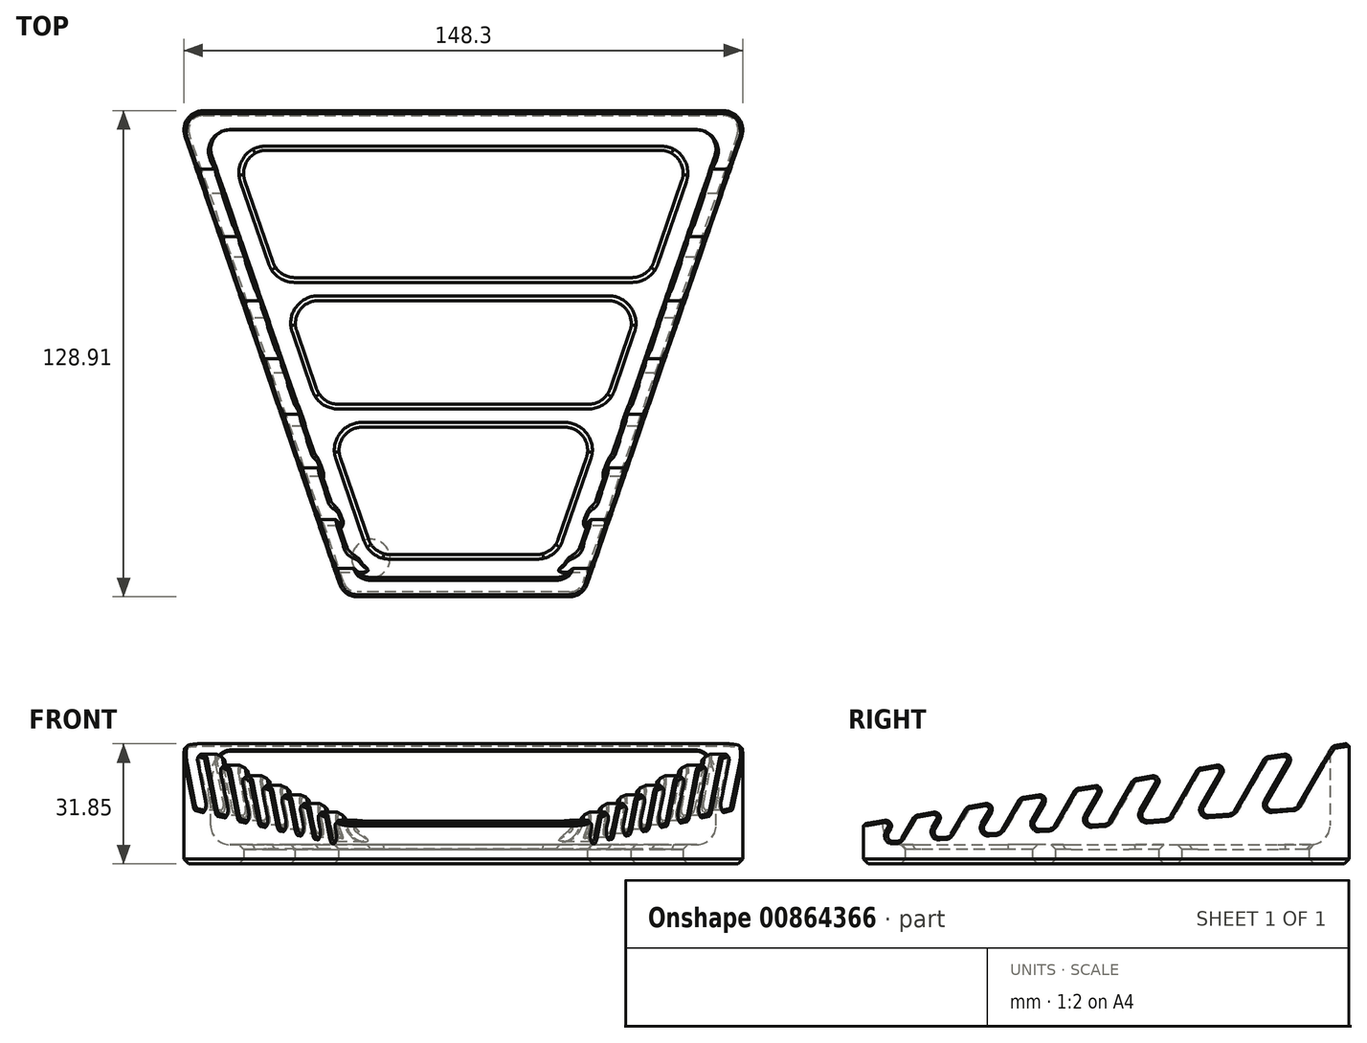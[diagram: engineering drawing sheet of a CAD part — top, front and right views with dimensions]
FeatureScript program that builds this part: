
annotation { "Feature Type Name" : "Feature", "Feature Type Description" : "" }
export const myFeature = defineFeature(function(context is Context, id is Id, definition is map)
    precondition{}
    {
        {
            var Q0;
            Q0=qCreatedBy(makeId("Top.planeOp"),FACE);
            var sketch = newSketch(context, id + "F0", { "sketchPlane" : qUnion([Q0])});
            skLineSegment(sketch, "E0", {"start": v(0, 200.12) * mm, "end": v(0, 0) * mm, "construction": true});
            skLineSegment(sketch, "E1", {"start": v(0, 0) * mm, "end": v(243.38, 0) * mm, "construction": true});
            skLineSegment(sketch, "E2", {"start": v(-76.2, 128.9) * mm, "end": v(76.2, 128.9) * mm});
            skLineSegment(sketch, "E3", {"start": v(76.2, 128.9) * mm, "end": v(31.75, 0) * mm});
            skLineSegment(sketch, "E4", {"start": v(31.75, 0) * mm, "end": v(-31.75, 0) * mm});
            skLineSegment(sketch, "E5", {"start": v(-31.75, 0) * mm, "end": v(-76.2, 128.9) * mm});
            skSolve(sketch);
        }
        {
            var Q0;
            Q0=makeQuery(id+"F0.imprint","IMPRINT",FACE,{"disambiguationData":[TD([[makeQuery(id+"F0.imprint","IMPRINT",EDGE,{"derivedFrom":sQuery(id+"F0.wireOp",EDGE,"E2")}),-1.0]])]});
            extrude(context, id + "F1", {"entities" : qUnion([Q0]), "depth" : 50.8 * mm, "offsetDistance" : 25.4 * mm});
        }
        {
            var Q0;
            Q0=qCreatedBy(makeId("Right.planeOp"),FACE);
            var sketch = newSketch(context, id + "F2", { "sketchPlane" : qUnion([Q0])});
            skLineSegment(sketch, "E6", {"start": v(0, 88.7) * mm, "end": v(0, 0) * mm, "construction": true});
            skLineSegment(sketch, "E7", {"start": v(0, 0) * mm, "end": v(187.78, 0) * mm, "construction": true});
            skCircle(sketch, "E8", {"center": v(114.24, 14.67) * mm, "radius": 14.67 * mm, "construction": true});
            skLineSegment(sketch, "E9", {"start": v(114.24, 14.67) * mm, "end": v(5.71, 5.71) * mm, "construction": true});
            skLineSegment(sketch, "E10", {"start": v(10.17, 2.13) * mm, "end": v(103.03, 5.2) * mm, "construction": true});
            skCircle(sketch, "E11", {"center": v(5.72, 5.71) * mm, "radius": 5.72 * mm, "construction": true});
            skLineSegment(sketch, "E12", {"start": v(111.83, 29.14) * mm, "end": v(4.78, 11.35) * mm, "construction": true});
            skSolve(sketch);
        }
        {
            var Q0;
            Q0=makeQuery(id+"F1.opExtrude","CAP_FACE",FACE,{"disambiguationData":[OSD([sQuery(id+"F0.wireOp",EDGE,"E2"),sQuery(id+"F0.wireOp",EDGE,"E3"),sQuery(id+"F0.wireOp",EDGE,"E4"),sQuery(id+"F0.wireOp",EDGE,"E5")])],"isStart":false});
            shell(context, id + "F3", {"entities" : qUnion([Q0]), "thickness" : 5.08 * mm});
        }
        {
            var Q0;
            Q0=makeQuery(id+"F3.opShell","OFFSET_EDGE",EDGE,{"disambiguationData":[OSD([sQuery(id+"F0.wireOp",EDGE,"E2"),sQuery(id+"F0.wireOp",EDGE,"E3")])]});
            var Q1;
            Q1=makeQuery(id+"F3.opShell","OFFSET_EDGE",EDGE,{"disambiguationData":[OSD([sQuery(id+"F0.wireOp",EDGE,"E3"),sQuery(id+"F0.wireOp",EDGE,"E4")])]});
            var Q2;
            Q2=makeQuery(id+"F3.opShell","OFFSET_EDGE",EDGE,{"disambiguationData":[OSD([sQuery(id+"F0.wireOp",EDGE,"E2"),sQuery(id+"F0.wireOp",EDGE,"E5")])]});
            var Q3;
            Q3=makeQuery(id+"F3.opShell","OFFSET_EDGE",EDGE,{"disambiguationData":[OSD([sQuery(id+"F0.wireOp",EDGE,"E4"),sQuery(id+"F0.wireOp",EDGE,"E5")])]});
            var Q4;
            Q4=makeQuery(id+"F1.opExtrude","SWEPT_EDGE",EDGE,{"disambiguationData":[OSD([sQuery(id+"F0.wireOp",EDGE,"E4"),sQuery(id+"F0.wireOp",EDGE,"E5")])]});
            var Q5;
            Q5=makeQuery(id+"F1.opExtrude","SWEPT_EDGE",EDGE,{"disambiguationData":[OSD([sQuery(id+"F0.wireOp",EDGE,"E3"),sQuery(id+"F0.wireOp",EDGE,"E4")])]});
            var Q6;
            Q6=makeQuery(id+"F1.opExtrude","SWEPT_EDGE",EDGE,{"disambiguationData":[OSD([sQuery(id+"F0.wireOp",EDGE,"E2"),sQuery(id+"F0.wireOp",EDGE,"E3")])]});
            var Q7;
            Q7=makeQuery(id+"F1.opExtrude","SWEPT_EDGE",EDGE,{"disambiguationData":[OSD([sQuery(id+"F0.wireOp",EDGE,"E2"),sQuery(id+"F0.wireOp",EDGE,"E5")])]});
            fillet(context, id + "F4", {"entities" : qUnion([Q0, Q1, Q2, Q3, Q4, Q5, Q6, Q7]), "radius" : 5.08 * mm, "tangentPropagation" : true, "allowEdgeOverflow" : false});
        }
        {
            var Q0;
            {var subQ0=sQuery(id+"F0.wireOp",EDGE,"E3");Q0=makeQuery(id+"F3.opShell","OFFSET_EDGE",EDGE,{"disambiguationData":[OSD([subQ0]),TDD([makeQuery(id+"F1.opExtrude","CAP_EDGE",EDGE,{"disambiguationData":[OSD([subQ0])],"isStart":true})])]});}
            fillet(context, id + "F5", {"entities" : qUnion([Q0]), "radius" : 5.08 * mm, "tangentPropagation" : true, "allowEdgeOverflow" : false});
        }
        {
            var Q0;
            Q0=qCreatedBy(makeId("Right.planeOp"),FACE);
            var sketch = newSketch(context, id + "F6", { "sketchPlane" : qUnion([Q0])});
            skLineSegment(sketch, "E13", {"start": v(0, 69.39) * mm, "end": v(0, 0) * mm, "construction": true});
            skLineSegment(sketch, "E14", {"start": v(0, 0) * mm, "end": v(193.07, 0) * mm, "construction": true});
            skLineSegment(sketch, "E15", {"start": v(14.91, 18.68) * mm, "end": v(7.52, 5.86) * mm, "construction": true});
            skLineSegment(sketch, "E16", {"start": v(28.35, 20.99) * mm, "end": v(20.22, 6.91) * mm, "construction": true});
            skLineSegment(sketch, "E17", {"start": v(42.35, 23.4) * mm, "end": v(33.46, 8) * mm, "construction": true});
            skLineSegment(sketch, "E18", {"start": v(56.86, 25.93) * mm, "end": v(47.17, 9.13) * mm, "construction": true});
            skLineSegment(sketch, "E19", {"start": v(71.98, 28.5) * mm, "end": v(61.49, 10.32) * mm, "construction": true});
            skLineSegment(sketch, "E20", {"start": v(88.27, 31.3) * mm, "end": v(76.89, 11.59) * mm, "construction": true});
            skLineSegment(sketch, "E21", {"start": v(105.77, 34.31) * mm, "end": v(93.44, 12.95) * mm, "construction": true});
            skLineSegment(sketch, "E22", {"start": v(121.34, 33.34) * mm, "end": v(110.38, 14.35) * mm, "construction": true});
            skLineSegment(sketch, "E23", {"start": v(124.53, 31.25) * mm, "end": v(141.6, 34.09) * mm});
            skLineSegment(sketch, "E24", {"start": v(141.6, 34.09) * mm, "end": v(141.6, 63.5) * mm});
            skLineSegment(sketch, "E25", {"start": v(141.6, 63.5) * mm, "end": v(-12.7, 63.5) * mm});
            skLineSegment(sketch, "E26", {"start": v(-12.7, 63.5) * mm, "end": v(-12.7, 8.45) * mm});
            skLineSegment(sketch, "E27", {"start": v(-12.7, 8.45) * mm, "end": v(8.88, 12.03) * mm});
            skLineSegment(sketch, "E28", {"start": v(124.53, 31.25) * mm, "end": v(115, 14.73) * mm});
            skLineSegment(sketch, "E29", {"start": v(115, 14.73) * mm, "end": v(105.76, 13.97) * mm});
            skLineSegment(sketch, "E30", {"start": v(105.76, 13.97) * mm, "end": v(114.8, 29.63) * mm});
            skLineSegment(sketch, "E31", {"start": v(106.69, 28.28) * mm, "end": v(98.06, 13.33) * mm});
            skLineSegment(sketch, "E32", {"start": v(98.06, 13.33) * mm, "end": v(88.82, 12.57) * mm});
            skLineSegment(sketch, "E33", {"start": v(88.82, 12.57) * mm, "end": v(96.96, 26.67) * mm});
            skLineSegment(sketch, "E34", {"start": v(88.85, 25.32) * mm, "end": v(81.12, 11.94) * mm});
            skLineSegment(sketch, "E35", {"start": v(81.12, 11.94) * mm, "end": v(72.65, 11.24) * mm});
            skLineSegment(sketch, "E36", {"start": v(72.65, 11.24) * mm, "end": v(79.93, 23.84) * mm});
            skLineSegment(sketch, "E37", {"start": v(71.82, 22.5) * mm, "end": v(64.95, 10.6) * mm});
            skLineSegment(sketch, "E38", {"start": v(64.95, 10.6) * mm, "end": v(58.02, 10.03) * mm});
            skLineSegment(sketch, "E39", {"start": v(58.02, 10.03) * mm, "end": v(64.52, 21.28) * mm});
            skLineSegment(sketch, "E40", {"start": v(50.32, 9.4) * mm, "end": v(44.01, 8.87) * mm});
            skLineSegment(sketch, "E41", {"start": v(44.01, 8.87) * mm, "end": v(49.76, 18.83) * mm});
            skLineSegment(sketch, "E42", {"start": v(41.65, 17.48) * mm, "end": v(36.31, 8.24) * mm});
            skLineSegment(sketch, "E43", {"start": v(36.31, 8.24) * mm, "end": v(30.61, 7.77) * mm});
            skLineSegment(sketch, "E44", {"start": v(30.61, 7.77) * mm, "end": v(35.64, 16.48) * mm});
            skLineSegment(sketch, "E45", {"start": v(27.53, 15.13) * mm, "end": v(22.91, 7.13) * mm});
            skLineSegment(sketch, "E46", {"start": v(22.91, 7.13) * mm, "end": v(17.53, 6.69) * mm});
            skLineSegment(sketch, "E47", {"start": v(17.53, 6.69) * mm, "end": v(21.86, 14.19) * mm});
            skLineSegment(sketch, "E48", {"start": v(13.75, 12.84) * mm, "end": v(9.83, 6.05) * mm});
            skLineSegment(sketch, "E49", {"start": v(9.83, 6.05) * mm, "end": v(8.1, 5.91) * mm});
            skLineSegment(sketch, "E50", {"start": v(6.66, 8.2) * mm, "end": v(8.88, 12.03) * mm});
            skLineSegment(sketch, "E51", {"start": v(13.75, 12.84) * mm, "end": v(21.86, 14.19) * mm});
            skLineSegment(sketch, "E52", {"start": v(27.53, 15.13) * mm, "end": v(35.64, 16.48) * mm});
            skLineSegment(sketch, "E53", {"start": v(41.65, 17.48) * mm, "end": v(49.76, 18.83) * mm});
            skLineSegment(sketch, "E54", {"start": v(56.4, 19.93) * mm, "end": v(64.52, 21.28) * mm});
            skLineSegment(sketch, "E55", {"start": v(71.82, 22.5) * mm, "end": v(79.93, 23.84) * mm});
            skLineSegment(sketch, "E56", {"start": v(88.85, 25.32) * mm, "end": v(96.96, 26.67) * mm});
            skLineSegment(sketch, "E57", {"start": v(106.69, 28.28) * mm, "end": v(114.8, 29.63) * mm});
            skLineSegment(sketch, "E58", {"start": v(56.4, 19.93) * mm, "end": v(50.32, 9.4) * mm});
            skPoint(sketch, "E59.visualSharp", {"position": v(5.2, 5.67) * mm});
            skArc(sketch, "E59.filletArc", {"start": v(6.66, 8.2) * mm, "mid": v(6.7, 6.62) * mm, "end": v(8.1, 5.91) * mm});
            skSolve(sketch);
        }
        {
            var Q0;
            Q0=qSketchRegion(id+"F6",true);
            extrude(context, id + "F7", {"entities" : qUnion([Q0]), "operationType" : NewBodyOperationType.REMOVE, "endBound" : BoundingType.THROUGH_ALL, "oppositeDirection" : true, "depth" : 25.4 * mm, "offsetDistance" : 25.4 * mm, "hasSecondDirection" : true, "secondDirectionBound" : SecondDirectionBoundingType.THROUGH_ALL, "secondDirectionOppositeDirection" : false, "secondDirectionDepth" : 25.4 * mm});
        }
        {
            var Q0;
            Q0=makeQuery(id+"F3.opShell","OFFSET_FACE",FACE,{"disambiguationData":[OSD([sQuery(id+"F0.wireOp",EDGE,"E2"),sQuery(id+"F0.wireOp",EDGE,"E3"),sQuery(id+"F0.wireOp",EDGE,"E4"),sQuery(id+"F0.wireOp",EDGE,"E5")])]});
            var sketch = newSketch(context, id + "F8", { "sketchPlane" : qUnion([Q0])});
            skLineSegment(sketch, "E60", {"start": v(-151.17, 0) * mm, "end": v(0, 0) * mm, "construction": true});
            skLineSegment(sketch, "E61", {"start": v(0, 0) * mm, "end": v(0, 307.09) * mm, "construction": true});
            skLineSegment(sketch, "E62", {"start": v(-23.78, 11.18) * mm, "end": v(23.78, 11.18) * mm});
            skLineSegment(sketch, "E63", {"start": v(23.78, 11.18) * mm, "end": v(35.43, 44.96) * mm});
            skLineSegment(sketch, "E64", {"start": v(60.77, 118.44) * mm, "end": v(-60.77, 118.44) * mm});
            skLineSegment(sketch, "E65", {"start": v(-60.77, 118.44) * mm, "end": v(-49.12, 84.65) * mm});
            skLineSegment(sketch, "E66", {"start": v(-36.48, 48) * mm, "end": v(36.48, 48) * mm, "construction": true});
            skLineSegment(sketch, "E67", {"start": v(-48.07, 81.6) * mm, "end": v(48.07, 81.6) * mm, "construction": true});
            skLineSegment(sketch, "E68", {"start": v(-35.43, 44.96) * mm, "end": v(35.43, 44.96) * mm});
            skLineSegment(sketch, "E69", {"start": v(-37.53, 51.05) * mm, "end": v(37.53, 51.05) * mm});
            skLineSegment(sketch, "E70", {"start": v(-47.02, 78.56) * mm, "end": v(47.02, 78.56) * mm});
            skLineSegment(sketch, "E71", {"start": v(-49.12, 84.65) * mm, "end": v(49.12, 84.65) * mm});
            skLineSegment(sketch, "E72.trimOffspring", {"start": v(-35.43, 44.96) * mm, "end": v(-23.78, 11.18) * mm});
            skLineSegment(sketch, "E73.trimOffspring", {"start": v(37.53, 51.05) * mm, "end": v(47.02, 78.56) * mm});
            skLineSegment(sketch, "E74.trimOffspring", {"start": v(49.12, 84.65) * mm, "end": v(60.77, 118.44) * mm});
            skLineSegment(sketch, "E75.trimOffspring", {"start": v(-47.02, 78.56) * mm, "end": v(-37.53, 51.05) * mm});
            skSolve(sketch);
        }
        {
            var Q0;
            Q0=makeQuery(id+"F8.imprint","IMPRINT",FACE,{"disambiguationData":[TD([[makeQuery(id+"F8.imprint","IMPRINT",EDGE,{"derivedFrom":sQuery(id+"F8.wireOp",EDGE,"E64")}),1.0]])]});
            var Q1;
            Q1=makeQuery(id+"F8.imprint","IMPRINT",FACE,{"disambiguationData":[TD([[makeQuery(id+"F8.imprint","IMPRINT",EDGE,{"derivedFrom":sQuery(id+"F8.wireOp",EDGE,"E69")}),1.0]])]});
            var Q2;
            Q2=makeQuery(id+"F8.imprint","IMPRINT",FACE,{"disambiguationData":[TD([[makeQuery(id+"F8.imprint","IMPRINT",EDGE,{"derivedFrom":sQuery(id+"F8.wireOp",EDGE,"E62")}),1.0]])]});
            extrude(context, id + "F9", {"entities" : qUnion([Q0, Q1, Q2]), "operationType" : NewBodyOperationType.REMOVE, "endBound" : BoundingType.THROUGH_ALL, "oppositeDirection" : true, "depth" : 25.4 * mm, "offsetDistance" : 25.4 * mm});
        }
        {
            var Q0;
            Q0=makeQuery(id+"F9.boolean.opBoolean","COPY",EDGE,{"derivedFrom":makeQuery(id+"F9.opExtrude","SWEPT_EDGE",EDGE,{"disambiguationData":[OSD([sQuery(id+"F8.wireOp",EDGE,"E64"),sQuery(id+"F8.wireOp",EDGE,"E74.trimOffspring")])]})});
            var Q1;
            Q1=makeQuery(id+"F9.boolean.opBoolean","COPY",EDGE,{"derivedFrom":makeQuery(id+"F9.opExtrude","SWEPT_EDGE",EDGE,{"disambiguationData":[OSD([sQuery(id+"F8.wireOp",EDGE,"E70"),sQuery(id+"F8.wireOp",EDGE,"E73.trimOffspring")])]})});
            var Q2;
            Q2=makeQuery(id+"F9.boolean.opBoolean","COPY",EDGE,{"derivedFrom":makeQuery(id+"F9.opExtrude","SWEPT_EDGE",EDGE,{"disambiguationData":[OSD([sQuery(id+"F8.wireOp",EDGE,"E63"),sQuery(id+"F8.wireOp",EDGE,"E68")])]})});
            var Q3;
            Q3=makeQuery(id+"F9.boolean.opBoolean","COPY",EDGE,{"derivedFrom":makeQuery(id+"F9.opExtrude","SWEPT_EDGE",EDGE,{"disambiguationData":[OSD([sQuery(id+"F8.wireOp",EDGE,"E62"),sQuery(id+"F8.wireOp",EDGE,"E63")])]})});
            var Q4;
            Q4=makeQuery(id+"F9.boolean.opBoolean","COPY",EDGE,{"derivedFrom":makeQuery(id+"F9.opExtrude","SWEPT_EDGE",EDGE,{"disambiguationData":[OSD([sQuery(id+"F8.wireOp",EDGE,"E69"),sQuery(id+"F8.wireOp",EDGE,"E73.trimOffspring")])]})});
            var Q5;
            Q5=makeQuery(id+"F9.boolean.opBoolean","COPY",EDGE,{"derivedFrom":makeQuery(id+"F9.opExtrude","SWEPT_EDGE",EDGE,{"disambiguationData":[OSD([sQuery(id+"F8.wireOp",EDGE,"E71"),sQuery(id+"F8.wireOp",EDGE,"E74.trimOffspring")])]})});
            var Q6;
            Q6=makeQuery(id+"F9.boolean.opBoolean","COPY",EDGE,{"derivedFrom":makeQuery(id+"F9.opExtrude","SWEPT_EDGE",EDGE,{"disambiguationData":[OSD([sQuery(id+"F8.wireOp",EDGE,"E62"),sQuery(id+"F8.wireOp",EDGE,"E72.trimOffspring")])]})});
            var Q7;
            Q7=makeQuery(id+"F9.boolean.opBoolean","COPY",EDGE,{"derivedFrom":makeQuery(id+"F9.opExtrude","SWEPT_EDGE",EDGE,{"disambiguationData":[OSD([sQuery(id+"F8.wireOp",EDGE,"E69"),sQuery(id+"F8.wireOp",EDGE,"E75.trimOffspring")])]})});
            var Q8;
            Q8=makeQuery(id+"F9.boolean.opBoolean","COPY",EDGE,{"derivedFrom":makeQuery(id+"F9.opExtrude","SWEPT_EDGE",EDGE,{"disambiguationData":[OSD([sQuery(id+"F8.wireOp",EDGE,"E65"),sQuery(id+"F8.wireOp",EDGE,"E71")])]})});
            var Q9;
            Q9=makeQuery(id+"F9.boolean.opBoolean","COPY",EDGE,{"derivedFrom":makeQuery(id+"F9.opExtrude","SWEPT_EDGE",EDGE,{"disambiguationData":[OSD([sQuery(id+"F8.wireOp",EDGE,"E64"),sQuery(id+"F8.wireOp",EDGE,"E65")])]})});
            var Q10;
            Q10=makeQuery(id+"F9.boolean.opBoolean","COPY",EDGE,{"derivedFrom":makeQuery(id+"F9.opExtrude","SWEPT_EDGE",EDGE,{"disambiguationData":[OSD([sQuery(id+"F8.wireOp",EDGE,"E70"),sQuery(id+"F8.wireOp",EDGE,"E75.trimOffspring")])]})});
            var Q11;
            Q11=makeQuery(id+"F9.boolean.opBoolean","COPY",EDGE,{"derivedFrom":makeQuery(id+"F9.opExtrude","SWEPT_EDGE",EDGE,{"disambiguationData":[OSD([sQuery(id+"F8.wireOp",EDGE,"E68"),sQuery(id+"F8.wireOp",EDGE,"E72.trimOffspring")])]})});
            fillet(context, id + "F10", {"entities" : qUnion([Q0, Q1, Q2, Q3, Q4, Q5, Q6, Q7, Q8, Q9, Q10, Q11]), "radius" : 6.1 * mm, "tangentPropagation" : true, "allowEdgeOverflow" : false});
        }
        {
            var Q0;
            {var subQ0=sQuery(id+"F0.wireOp",EDGE,"E5");var subQ1=sQuery(id+"F6.wireOp",EDGE,"E49");var subQ2=sQuery(id+"F6.wireOp",EDGE,"E48");Q0=makeQuery(id+"F7.boolean.opBoolean","COPY",EDGE,{"disambiguationData":[TD([makeQuery(id+"F1.opExtrude","SWEPT_FACE",FACE,{"disambiguationData":[OSD([subQ0])]})])],"derivedFrom":makeQuery(id+"F7.opExtrude","SWEPT_EDGE",EDGE,{"disambiguationData":[OSD([subQ2,subQ1])]})});}
            var Q1;
            {var subQ0=sQuery(id+"F0.wireOp",EDGE,"E5");var subQ1=sQuery(id+"F6.wireOp",EDGE,"E45");var subQ2=sQuery(id+"F6.wireOp",EDGE,"E46");Q1=makeQuery(id+"F7.boolean.opBoolean","COPY",EDGE,{"disambiguationData":[TD([makeQuery(id+"F1.opExtrude","SWEPT_FACE",FACE,{"disambiguationData":[OSD([subQ0])]})])],"derivedFrom":makeQuery(id+"F7.opExtrude","SWEPT_EDGE",EDGE,{"disambiguationData":[OSD([subQ1,subQ2])]})});}
            var Q2;
            {var subQ0=sQuery(id+"F0.wireOp",EDGE,"E5");var subQ1=sQuery(id+"F6.wireOp",EDGE,"E46");var subQ2=sQuery(id+"F6.wireOp",EDGE,"E47");Q2=makeQuery(id+"F7.boolean.opBoolean","COPY",EDGE,{"disambiguationData":[TD([makeQuery(id+"F1.opExtrude","SWEPT_FACE",FACE,{"disambiguationData":[OSD([subQ0])]})])],"derivedFrom":makeQuery(id+"F7.opExtrude","SWEPT_EDGE",EDGE,{"disambiguationData":[OSD([subQ1,subQ2])]})});}
            var Q3;
            {var subQ0=sQuery(id+"F0.wireOp",EDGE,"E5");var subQ1=sQuery(id+"F6.wireOp",EDGE,"E44");var subQ2=sQuery(id+"F6.wireOp",EDGE,"E43");Q3=makeQuery(id+"F7.boolean.opBoolean","COPY",EDGE,{"disambiguationData":[TD([makeQuery(id+"F1.opExtrude","SWEPT_FACE",FACE,{"disambiguationData":[OSD([subQ0])]})])],"derivedFrom":makeQuery(id+"F7.opExtrude","SWEPT_EDGE",EDGE,{"disambiguationData":[OSD([subQ2,subQ1])]})});}
            var Q4;
            {var subQ0=sQuery(id+"F0.wireOp",EDGE,"E5");var subQ1=sQuery(id+"F6.wireOp",EDGE,"E42");var subQ2=sQuery(id+"F6.wireOp",EDGE,"E43");Q4=makeQuery(id+"F7.boolean.opBoolean","COPY",EDGE,{"disambiguationData":[TD([makeQuery(id+"F1.opExtrude","SWEPT_FACE",FACE,{"disambiguationData":[OSD([subQ0])]})])],"derivedFrom":makeQuery(id+"F7.opExtrude","SWEPT_EDGE",EDGE,{"disambiguationData":[OSD([subQ1,subQ2])]})});}
            var Q5;
            {var subQ0=sQuery(id+"F0.wireOp",EDGE,"E5");var subQ1=sQuery(id+"F6.wireOp",EDGE,"E40");var subQ2=sQuery(id+"F6.wireOp",EDGE,"E41");Q5=makeQuery(id+"F7.boolean.opBoolean","COPY",EDGE,{"disambiguationData":[TD([makeQuery(id+"F1.opExtrude","SWEPT_FACE",FACE,{"disambiguationData":[OSD([subQ0])]})])],"derivedFrom":makeQuery(id+"F7.opExtrude","SWEPT_EDGE",EDGE,{"disambiguationData":[OSD([subQ1,subQ2])]})});}
            var Q6;
            {var subQ0=sQuery(id+"F0.wireOp",EDGE,"E5");var subQ1=sQuery(id+"F6.wireOp",EDGE,"E40");var subQ2=sQuery(id+"F6.wireOp",EDGE,"E58");Q6=makeQuery(id+"F7.boolean.opBoolean","COPY",EDGE,{"disambiguationData":[TD([makeQuery(id+"F1.opExtrude","SWEPT_FACE",FACE,{"disambiguationData":[OSD([subQ0])]})])],"derivedFrom":makeQuery(id+"F7.opExtrude","SWEPT_EDGE",EDGE,{"disambiguationData":[OSD([subQ1,subQ2])]})});}
            var Q7;
            {var subQ0=sQuery(id+"F0.wireOp",EDGE,"E5");var subQ1=sQuery(id+"F6.wireOp",EDGE,"E37");var subQ2=sQuery(id+"F6.wireOp",EDGE,"E38");Q7=makeQuery(id+"F7.boolean.opBoolean","COPY",EDGE,{"disambiguationData":[TD([makeQuery(id+"F1.opExtrude","SWEPT_FACE",FACE,{"disambiguationData":[OSD([subQ0])]})])],"derivedFrom":makeQuery(id+"F7.opExtrude","SWEPT_EDGE",EDGE,{"disambiguationData":[OSD([subQ1,subQ2])]})});}
            var Q8;
            {var subQ0=sQuery(id+"F0.wireOp",EDGE,"E5");var subQ1=sQuery(id+"F6.wireOp",EDGE,"E39");var subQ2=sQuery(id+"F6.wireOp",EDGE,"E38");Q8=makeQuery(id+"F7.boolean.opBoolean","COPY",EDGE,{"disambiguationData":[TD([makeQuery(id+"F1.opExtrude","SWEPT_FACE",FACE,{"disambiguationData":[OSD([subQ0])]})])],"derivedFrom":makeQuery(id+"F7.opExtrude","SWEPT_EDGE",EDGE,{"disambiguationData":[OSD([subQ2,subQ1])]})});}
            var Q9;
            {var subQ0=sQuery(id+"F0.wireOp",EDGE,"E5");var subQ1=sQuery(id+"F6.wireOp",EDGE,"E35");var subQ2=sQuery(id+"F6.wireOp",EDGE,"E36");Q9=makeQuery(id+"F7.boolean.opBoolean","COPY",EDGE,{"disambiguationData":[TD([makeQuery(id+"F1.opExtrude","SWEPT_FACE",FACE,{"disambiguationData":[OSD([subQ0])]})])],"derivedFrom":makeQuery(id+"F7.opExtrude","SWEPT_EDGE",EDGE,{"disambiguationData":[OSD([subQ1,subQ2])]})});}
            var Q10;
            {var subQ0=sQuery(id+"F0.wireOp",EDGE,"E5");var subQ1=sQuery(id+"F6.wireOp",EDGE,"E34");var subQ2=sQuery(id+"F6.wireOp",EDGE,"E35");Q10=makeQuery(id+"F7.boolean.opBoolean","COPY",EDGE,{"disambiguationData":[TD([makeQuery(id+"F1.opExtrude","SWEPT_FACE",FACE,{"disambiguationData":[OSD([subQ0])]})])],"derivedFrom":makeQuery(id+"F7.opExtrude","SWEPT_EDGE",EDGE,{"disambiguationData":[OSD([subQ1,subQ2])]})});}
            var Q11;
            {var subQ0=sQuery(id+"F0.wireOp",EDGE,"E5");var subQ1=sQuery(id+"F6.wireOp",EDGE,"E31");var subQ2=sQuery(id+"F6.wireOp",EDGE,"E32");Q11=makeQuery(id+"F7.boolean.opBoolean","COPY",EDGE,{"disambiguationData":[TD([makeQuery(id+"F1.opExtrude","SWEPT_FACE",FACE,{"disambiguationData":[OSD([subQ0])]})])],"derivedFrom":makeQuery(id+"F7.opExtrude","SWEPT_EDGE",EDGE,{"disambiguationData":[OSD([subQ1,subQ2])]})});}
            var Q12;
            {var subQ0=sQuery(id+"F0.wireOp",EDGE,"E5");var subQ1=sQuery(id+"F6.wireOp",EDGE,"E32");var subQ2=sQuery(id+"F6.wireOp",EDGE,"E33");Q12=makeQuery(id+"F7.boolean.opBoolean","COPY",EDGE,{"disambiguationData":[TD([makeQuery(id+"F1.opExtrude","SWEPT_FACE",FACE,{"disambiguationData":[OSD([subQ0])]})])],"derivedFrom":makeQuery(id+"F7.opExtrude","SWEPT_EDGE",EDGE,{"disambiguationData":[OSD([subQ1,subQ2])]})});}
            var Q13;
            {var subQ0=sQuery(id+"F0.wireOp",EDGE,"E5");var subQ1=sQuery(id+"F6.wireOp",EDGE,"E29");var subQ2=sQuery(id+"F6.wireOp",EDGE,"E30");Q13=makeQuery(id+"F7.boolean.opBoolean","COPY",EDGE,{"disambiguationData":[TD([makeQuery(id+"F1.opExtrude","SWEPT_FACE",FACE,{"disambiguationData":[OSD([subQ0])]})])],"derivedFrom":makeQuery(id+"F7.opExtrude","SWEPT_EDGE",EDGE,{"disambiguationData":[OSD([subQ1,subQ2])]})});}
            var Q14;
            {var subQ0=sQuery(id+"F0.wireOp",EDGE,"E5");var subQ1=sQuery(id+"F6.wireOp",EDGE,"E29");var subQ2=sQuery(id+"F6.wireOp",EDGE,"E28");Q14=makeQuery(id+"F7.boolean.opBoolean","COPY",EDGE,{"disambiguationData":[TD([makeQuery(id+"F1.opExtrude","SWEPT_FACE",FACE,{"disambiguationData":[OSD([subQ0])]})])],"derivedFrom":makeQuery(id+"F7.opExtrude","SWEPT_EDGE",EDGE,{"disambiguationData":[OSD([subQ2,subQ1])]})});}
            var Q15;
            {var subQ0=sQuery(id+"F0.wireOp",EDGE,"E3");var subQ1=sQuery(id+"F6.wireOp",EDGE,"E29");var subQ2=sQuery(id+"F6.wireOp",EDGE,"E30");Q15=makeQuery(id+"F7.boolean.opBoolean","COPY",EDGE,{"disambiguationData":[TD([makeQuery(id+"F1.opExtrude","SWEPT_FACE",FACE,{"disambiguationData":[OSD([subQ0])]})])],"derivedFrom":makeQuery(id+"F7.opExtrude","SWEPT_EDGE",EDGE,{"disambiguationData":[OSD([subQ1,subQ2])]})});}
            var Q16;
            {var subQ0=sQuery(id+"F0.wireOp",EDGE,"E3");var subQ1=sQuery(id+"F6.wireOp",EDGE,"E32");var subQ2=sQuery(id+"F6.wireOp",EDGE,"E33");Q16=makeQuery(id+"F7.boolean.opBoolean","COPY",EDGE,{"disambiguationData":[TD([makeQuery(id+"F1.opExtrude","SWEPT_FACE",FACE,{"disambiguationData":[OSD([subQ0])]})])],"derivedFrom":makeQuery(id+"F7.opExtrude","SWEPT_EDGE",EDGE,{"disambiguationData":[OSD([subQ1,subQ2])]})});}
            var Q17;
            {var subQ0=sQuery(id+"F0.wireOp",EDGE,"E3");var subQ1=sQuery(id+"F6.wireOp",EDGE,"E32");var subQ2=sQuery(id+"F6.wireOp",EDGE,"E31");Q17=makeQuery(id+"F7.boolean.opBoolean","COPY",EDGE,{"disambiguationData":[TD([makeQuery(id+"F1.opExtrude","SWEPT_FACE",FACE,{"disambiguationData":[OSD([subQ0])]})])],"derivedFrom":makeQuery(id+"F7.opExtrude","SWEPT_EDGE",EDGE,{"disambiguationData":[OSD([subQ2,subQ1])]})});}
            var Q18;
            {var subQ0=sQuery(id+"F0.wireOp",EDGE,"E3");var subQ1=sQuery(id+"F6.wireOp",EDGE,"E28");var subQ2=sQuery(id+"F6.wireOp",EDGE,"E29");Q18=makeQuery(id+"F7.boolean.opBoolean","COPY",EDGE,{"disambiguationData":[TD([makeQuery(id+"F1.opExtrude","SWEPT_FACE",FACE,{"disambiguationData":[OSD([subQ0])]})])],"derivedFrom":makeQuery(id+"F7.opExtrude","SWEPT_EDGE",EDGE,{"disambiguationData":[OSD([subQ1,subQ2])]})});}
            var Q19;
            {var subQ0=sQuery(id+"F0.wireOp",EDGE,"E3");var subQ1=sQuery(id+"F6.wireOp",EDGE,"E34");var subQ2=sQuery(id+"F6.wireOp",EDGE,"E35");Q19=makeQuery(id+"F7.boolean.opBoolean","COPY",EDGE,{"disambiguationData":[TD([makeQuery(id+"F1.opExtrude","SWEPT_FACE",FACE,{"disambiguationData":[OSD([subQ0])]})])],"derivedFrom":makeQuery(id+"F7.opExtrude","SWEPT_EDGE",EDGE,{"disambiguationData":[OSD([subQ1,subQ2])]})});}
            var Q20;
            {var subQ0=sQuery(id+"F0.wireOp",EDGE,"E3");var subQ1=sQuery(id+"F6.wireOp",EDGE,"E37");var subQ2=sQuery(id+"F6.wireOp",EDGE,"E38");Q20=makeQuery(id+"F7.boolean.opBoolean","COPY",EDGE,{"disambiguationData":[TD([makeQuery(id+"F1.opExtrude","SWEPT_FACE",FACE,{"disambiguationData":[OSD([subQ0])]})])],"derivedFrom":makeQuery(id+"F7.opExtrude","SWEPT_EDGE",EDGE,{"disambiguationData":[OSD([subQ1,subQ2])]})});}
            var Q21;
            {var subQ0=sQuery(id+"F0.wireOp",EDGE,"E3");var subQ1=sQuery(id+"F6.wireOp",EDGE,"E35");var subQ2=sQuery(id+"F6.wireOp",EDGE,"E36");Q21=makeQuery(id+"F7.boolean.opBoolean","COPY",EDGE,{"disambiguationData":[TD([makeQuery(id+"F1.opExtrude","SWEPT_FACE",FACE,{"disambiguationData":[OSD([subQ0])]})])],"derivedFrom":makeQuery(id+"F7.opExtrude","SWEPT_EDGE",EDGE,{"disambiguationData":[OSD([subQ1,subQ2])]})});}
            var Q22;
            {var subQ0=sQuery(id+"F0.wireOp",EDGE,"E3");var subQ1=sQuery(id+"F6.wireOp",EDGE,"E38");var subQ2=sQuery(id+"F6.wireOp",EDGE,"E39");Q22=makeQuery(id+"F7.boolean.opBoolean","COPY",EDGE,{"disambiguationData":[TD([makeQuery(id+"F1.opExtrude","SWEPT_FACE",FACE,{"disambiguationData":[OSD([subQ0])]})])],"derivedFrom":makeQuery(id+"F7.opExtrude","SWEPT_EDGE",EDGE,{"disambiguationData":[OSD([subQ1,subQ2])]})});}
            var Q23;
            {var subQ0=sQuery(id+"F0.wireOp",EDGE,"E3");var subQ1=sQuery(id+"F6.wireOp",EDGE,"E40");var subQ2=sQuery(id+"F6.wireOp",EDGE,"E41");Q23=makeQuery(id+"F7.boolean.opBoolean","COPY",EDGE,{"disambiguationData":[TD([makeQuery(id+"F1.opExtrude","SWEPT_FACE",FACE,{"disambiguationData":[OSD([subQ0])]})])],"derivedFrom":makeQuery(id+"F7.opExtrude","SWEPT_EDGE",EDGE,{"disambiguationData":[OSD([subQ1,subQ2])]})});}
            var Q24;
            {var subQ0=sQuery(id+"F0.wireOp",EDGE,"E3");var subQ1=sQuery(id+"F6.wireOp",EDGE,"E43");var subQ2=sQuery(id+"F6.wireOp",EDGE,"E44");Q24=makeQuery(id+"F7.boolean.opBoolean","COPY",EDGE,{"disambiguationData":[TD([makeQuery(id+"F1.opExtrude","SWEPT_FACE",FACE,{"disambiguationData":[OSD([subQ0])]})])],"derivedFrom":makeQuery(id+"F7.opExtrude","SWEPT_EDGE",EDGE,{"disambiguationData":[OSD([subQ1,subQ2])]})});}
            var Q25;
            {var subQ0=sQuery(id+"F0.wireOp",EDGE,"E3");var subQ1=sQuery(id+"F6.wireOp",EDGE,"E42");var subQ2=sQuery(id+"F6.wireOp",EDGE,"E43");Q25=makeQuery(id+"F7.boolean.opBoolean","COPY",EDGE,{"disambiguationData":[TD([makeQuery(id+"F1.opExtrude","SWEPT_FACE",FACE,{"disambiguationData":[OSD([subQ0])]})])],"derivedFrom":makeQuery(id+"F7.opExtrude","SWEPT_EDGE",EDGE,{"disambiguationData":[OSD([subQ1,subQ2])]})});}
            var Q26;
            {var subQ0=sQuery(id+"F0.wireOp",EDGE,"E3");var subQ1=sQuery(id+"F6.wireOp",EDGE,"E58");var subQ2=sQuery(id+"F6.wireOp",EDGE,"E40");Q26=makeQuery(id+"F7.boolean.opBoolean","COPY",EDGE,{"disambiguationData":[TD([makeQuery(id+"F1.opExtrude","SWEPT_FACE",FACE,{"disambiguationData":[OSD([subQ0])]})])],"derivedFrom":makeQuery(id+"F7.opExtrude","SWEPT_EDGE",EDGE,{"disambiguationData":[OSD([subQ2,subQ1])]})});}
            var Q27;
            {var subQ0=sQuery(id+"F0.wireOp",EDGE,"E3");var subQ1=sQuery(id+"F6.wireOp",EDGE,"E45");var subQ2=sQuery(id+"F6.wireOp",EDGE,"E46");Q27=makeQuery(id+"F7.boolean.opBoolean","COPY",EDGE,{"disambiguationData":[TD([makeQuery(id+"F1.opExtrude","SWEPT_FACE",FACE,{"disambiguationData":[OSD([subQ0])]})])],"derivedFrom":makeQuery(id+"F7.opExtrude","SWEPT_EDGE",EDGE,{"disambiguationData":[OSD([subQ1,subQ2])]})});}
            var Q28;
            {var subQ0=sQuery(id+"F0.wireOp",EDGE,"E3");var subQ1=sQuery(id+"F6.wireOp",EDGE,"E47");var subQ2=sQuery(id+"F6.wireOp",EDGE,"E46");Q28=makeQuery(id+"F7.boolean.opBoolean","COPY",EDGE,{"disambiguationData":[TD([makeQuery(id+"F1.opExtrude","SWEPT_FACE",FACE,{"disambiguationData":[OSD([subQ0])]})])],"derivedFrom":makeQuery(id+"F7.opExtrude","SWEPT_EDGE",EDGE,{"disambiguationData":[OSD([subQ2,subQ1])]})});}
            var Q29;
            {var subQ0=sQuery(id+"F0.wireOp",EDGE,"E3");var subQ1=sQuery(id+"F6.wireOp",EDGE,"E48");var subQ2=sQuery(id+"F6.wireOp",EDGE,"E49");Q29=makeQuery(id+"F7.boolean.opBoolean","COPY",EDGE,{"disambiguationData":[TD([makeQuery(id+"F1.opExtrude","SWEPT_FACE",FACE,{"disambiguationData":[OSD([subQ0])]})])],"derivedFrom":makeQuery(id+"F7.opExtrude","SWEPT_EDGE",EDGE,{"disambiguationData":[OSD([subQ1,subQ2])]})});}
            var Q30;
            {var subQ0=sQuery(id+"F0.wireOp",EDGE,"E3");var subQ1=sQuery(id+"F6.wireOp",EDGE,"E27");var subQ2=sQuery(id+"F6.wireOp",EDGE,"E50");Q30=makeQuery(id+"F7.boolean.opBoolean","COPY",EDGE,{"disambiguationData":[TD([makeQuery(id+"F1.opExtrude","SWEPT_FACE",FACE,{"disambiguationData":[OSD([subQ0])]})])],"derivedFrom":makeQuery(id+"F7.opExtrude","SWEPT_EDGE",EDGE,{"disambiguationData":[OSD([subQ1,subQ2])]})});}
            var Q31;
            {var subQ0=sQuery(id+"F0.wireOp",EDGE,"E3");var subQ1=sQuery(id+"F6.wireOp",EDGE,"E48");var subQ2=sQuery(id+"F6.wireOp",EDGE,"E51");Q31=makeQuery(id+"F7.boolean.opBoolean","COPY",EDGE,{"disambiguationData":[TD([makeQuery(id+"F1.opExtrude","SWEPT_FACE",FACE,{"disambiguationData":[OSD([subQ0])]})])],"derivedFrom":makeQuery(id+"F7.opExtrude","SWEPT_EDGE",EDGE,{"disambiguationData":[OSD([subQ1,subQ2])]})});}
            var Q32;
            {var subQ0=sQuery(id+"F0.wireOp",EDGE,"E3");var subQ1=sQuery(id+"F6.wireOp",EDGE,"E47");var subQ2=sQuery(id+"F6.wireOp",EDGE,"E51");Q32=makeQuery(id+"F7.boolean.opBoolean","COPY",EDGE,{"disambiguationData":[TD([makeQuery(id+"F1.opExtrude","SWEPT_FACE",FACE,{"disambiguationData":[OSD([subQ0])]})])],"derivedFrom":makeQuery(id+"F7.opExtrude","SWEPT_EDGE",EDGE,{"disambiguationData":[OSD([subQ1,subQ2])]})});}
            var Q33;
            {var subQ0=sQuery(id+"F0.wireOp",EDGE,"E3");var subQ1=sQuery(id+"F6.wireOp",EDGE,"E52");var subQ2=sQuery(id+"F6.wireOp",EDGE,"E45");Q33=makeQuery(id+"F7.boolean.opBoolean","COPY",EDGE,{"disambiguationData":[TD([makeQuery(id+"F1.opExtrude","SWEPT_FACE",FACE,{"disambiguationData":[OSD([subQ0])]})])],"derivedFrom":makeQuery(id+"F7.opExtrude","SWEPT_EDGE",EDGE,{"disambiguationData":[OSD([subQ2,subQ1])]})});}
            var Q34;
            {var subQ0=sQuery(id+"F0.wireOp",EDGE,"E3");var subQ1=sQuery(id+"F6.wireOp",EDGE,"E52");var subQ2=sQuery(id+"F6.wireOp",EDGE,"E44");Q34=makeQuery(id+"F7.boolean.opBoolean","COPY",EDGE,{"disambiguationData":[TD([makeQuery(id+"F1.opExtrude","SWEPT_FACE",FACE,{"disambiguationData":[OSD([subQ0])]})])],"derivedFrom":makeQuery(id+"F7.opExtrude","SWEPT_EDGE",EDGE,{"disambiguationData":[OSD([subQ2,subQ1])]})});}
            var Q35;
            {var subQ0=sQuery(id+"F0.wireOp",EDGE,"E3");var subQ1=sQuery(id+"F6.wireOp",EDGE,"E42");var subQ2=sQuery(id+"F6.wireOp",EDGE,"E53");Q35=makeQuery(id+"F7.boolean.opBoolean","COPY",EDGE,{"disambiguationData":[TD([makeQuery(id+"F1.opExtrude","SWEPT_FACE",FACE,{"disambiguationData":[OSD([subQ0])]})])],"derivedFrom":makeQuery(id+"F7.opExtrude","SWEPT_EDGE",EDGE,{"disambiguationData":[OSD([subQ1,subQ2])]})});}
            var Q36;
            {var subQ0=sQuery(id+"F0.wireOp",EDGE,"E3");var subQ1=sQuery(id+"F6.wireOp",EDGE,"E53");var subQ2=sQuery(id+"F6.wireOp",EDGE,"E41");Q36=makeQuery(id+"F7.boolean.opBoolean","COPY",EDGE,{"disambiguationData":[TD([makeQuery(id+"F1.opExtrude","SWEPT_FACE",FACE,{"disambiguationData":[OSD([subQ0])]})])],"derivedFrom":makeQuery(id+"F7.opExtrude","SWEPT_EDGE",EDGE,{"disambiguationData":[OSD([subQ2,subQ1])]})});}
            var Q37;
            {var subQ0=sQuery(id+"F0.wireOp",EDGE,"E3");var subQ1=sQuery(id+"F6.wireOp",EDGE,"E58");var subQ2=sQuery(id+"F6.wireOp",EDGE,"E54");Q37=makeQuery(id+"F7.boolean.opBoolean","COPY",EDGE,{"disambiguationData":[TD([makeQuery(id+"F1.opExtrude","SWEPT_FACE",FACE,{"disambiguationData":[OSD([subQ0])]})])],"derivedFrom":makeQuery(id+"F7.opExtrude","SWEPT_EDGE",EDGE,{"disambiguationData":[OSD([subQ2,subQ1])]})});}
            var Q38;
            {var subQ0=sQuery(id+"F0.wireOp",EDGE,"E3");var subQ1=sQuery(id+"F6.wireOp",EDGE,"E39");var subQ2=sQuery(id+"F6.wireOp",EDGE,"E54");Q38=makeQuery(id+"F7.boolean.opBoolean","COPY",EDGE,{"disambiguationData":[TD([makeQuery(id+"F1.opExtrude","SWEPT_FACE",FACE,{"disambiguationData":[OSD([subQ0])]})])],"derivedFrom":makeQuery(id+"F7.opExtrude","SWEPT_EDGE",EDGE,{"disambiguationData":[OSD([subQ1,subQ2])]})});}
            var Q39;
            {var subQ0=sQuery(id+"F0.wireOp",EDGE,"E3");var subQ1=sQuery(id+"F6.wireOp",EDGE,"E37");var subQ2=sQuery(id+"F6.wireOp",EDGE,"E55");Q39=makeQuery(id+"F7.boolean.opBoolean","COPY",EDGE,{"disambiguationData":[TD([makeQuery(id+"F1.opExtrude","SWEPT_FACE",FACE,{"disambiguationData":[OSD([subQ0])]})])],"derivedFrom":makeQuery(id+"F7.opExtrude","SWEPT_EDGE",EDGE,{"disambiguationData":[OSD([subQ1,subQ2])]})});}
            var Q40;
            {var subQ0=sQuery(id+"F0.wireOp",EDGE,"E3");var subQ1=sQuery(id+"F6.wireOp",EDGE,"E36");var subQ2=sQuery(id+"F6.wireOp",EDGE,"E55");Q40=makeQuery(id+"F7.boolean.opBoolean","COPY",EDGE,{"disambiguationData":[TD([makeQuery(id+"F1.opExtrude","SWEPT_FACE",FACE,{"disambiguationData":[OSD([subQ0])]})])],"derivedFrom":makeQuery(id+"F7.opExtrude","SWEPT_EDGE",EDGE,{"disambiguationData":[OSD([subQ1,subQ2])]})});}
            var Q41;
            {var subQ0=sQuery(id+"F0.wireOp",EDGE,"E3");var subQ1=sQuery(id+"F6.wireOp",EDGE,"E34");var subQ2=sQuery(id+"F6.wireOp",EDGE,"E56");Q41=makeQuery(id+"F7.boolean.opBoolean","COPY",EDGE,{"disambiguationData":[TD([makeQuery(id+"F1.opExtrude","SWEPT_FACE",FACE,{"disambiguationData":[OSD([subQ0])]})])],"derivedFrom":makeQuery(id+"F7.opExtrude","SWEPT_EDGE",EDGE,{"disambiguationData":[OSD([subQ1,subQ2])]})});}
            var Q42;
            {var subQ0=sQuery(id+"F0.wireOp",EDGE,"E3");var subQ1=sQuery(id+"F6.wireOp",EDGE,"E33");var subQ2=sQuery(id+"F6.wireOp",EDGE,"E56");Q42=makeQuery(id+"F7.boolean.opBoolean","COPY",EDGE,{"disambiguationData":[TD([makeQuery(id+"F1.opExtrude","SWEPT_FACE",FACE,{"disambiguationData":[OSD([subQ0])]})])],"derivedFrom":makeQuery(id+"F7.opExtrude","SWEPT_EDGE",EDGE,{"disambiguationData":[OSD([subQ1,subQ2])]})});}
            var Q43;
            {var subQ0=sQuery(id+"F0.wireOp",EDGE,"E3");var subQ1=sQuery(id+"F6.wireOp",EDGE,"E57");var subQ2=sQuery(id+"F6.wireOp",EDGE,"E31");Q43=makeQuery(id+"F7.boolean.opBoolean","COPY",EDGE,{"disambiguationData":[TD([makeQuery(id+"F1.opExtrude","SWEPT_FACE",FACE,{"disambiguationData":[OSD([subQ0])]})])],"derivedFrom":makeQuery(id+"F7.opExtrude","SWEPT_EDGE",EDGE,{"disambiguationData":[OSD([subQ2,subQ1])]})});}
            var Q44;
            {var subQ0=sQuery(id+"F0.wireOp",EDGE,"E3");var subQ1=sQuery(id+"F6.wireOp",EDGE,"E57");var subQ2=sQuery(id+"F6.wireOp",EDGE,"E30");Q44=makeQuery(id+"F7.boolean.opBoolean","COPY",EDGE,{"disambiguationData":[TD([makeQuery(id+"F1.opExtrude","SWEPT_FACE",FACE,{"disambiguationData":[OSD([subQ0])]})])],"derivedFrom":makeQuery(id+"F7.opExtrude","SWEPT_EDGE",EDGE,{"disambiguationData":[OSD([subQ2,subQ1])]})});}
            var Q45;
            {var subQ0=sQuery(id+"F0.wireOp",EDGE,"E3");var subQ2=sQuery(id+"F6.wireOp",EDGE,"E23");var subQ3=sQuery(id+"F6.wireOp",EDGE,"E28");Q45=makeQuery(id+"F7.boolean.opBoolean","COPY",EDGE,{"disambiguationData":[TD([makeQuery(id+"F1.opExtrude","SWEPT_FACE",FACE,{"disambiguationData":[OSD([subQ0])]})])],"derivedFrom":makeQuery(id+"F7.opExtrude","SWEPT_EDGE",EDGE,{"disambiguationData":[OSD([subQ2,subQ3])]})});}
            var Q46;
            {var subQ0=sQuery(id+"F0.wireOp",EDGE,"E5");var subQ2=sQuery(id+"F6.wireOp",EDGE,"E23");var subQ3=sQuery(id+"F6.wireOp",EDGE,"E28");Q46=makeQuery(id+"F7.boolean.opBoolean","COPY",EDGE,{"disambiguationData":[TD([makeQuery(id+"F1.opExtrude","SWEPT_FACE",FACE,{"disambiguationData":[OSD([subQ0])]})])],"derivedFrom":makeQuery(id+"F7.opExtrude","SWEPT_EDGE",EDGE,{"disambiguationData":[OSD([subQ2,subQ3])]})});}
            var Q47;
            {var subQ0=sQuery(id+"F0.wireOp",EDGE,"E5");var subQ1=sQuery(id+"F6.wireOp",EDGE,"E30");var subQ2=sQuery(id+"F6.wireOp",EDGE,"E57");Q47=makeQuery(id+"F7.boolean.opBoolean","COPY",EDGE,{"disambiguationData":[TD([makeQuery(id+"F1.opExtrude","SWEPT_FACE",FACE,{"disambiguationData":[OSD([subQ0])]})])],"derivedFrom":makeQuery(id+"F7.opExtrude","SWEPT_EDGE",EDGE,{"disambiguationData":[OSD([subQ1,subQ2])]})});}
            var Q48;
            {var subQ0=sQuery(id+"F0.wireOp",EDGE,"E5");var subQ1=sQuery(id+"F6.wireOp",EDGE,"E31");var subQ2=sQuery(id+"F6.wireOp",EDGE,"E57");Q48=makeQuery(id+"F7.boolean.opBoolean","COPY",EDGE,{"disambiguationData":[TD([makeQuery(id+"F1.opExtrude","SWEPT_FACE",FACE,{"disambiguationData":[OSD([subQ0])]})])],"derivedFrom":makeQuery(id+"F7.opExtrude","SWEPT_EDGE",EDGE,{"disambiguationData":[OSD([subQ1,subQ2])]})});}
            var Q49;
            {var subQ0=sQuery(id+"F0.wireOp",EDGE,"E5");var subQ1=sQuery(id+"F6.wireOp",EDGE,"E33");var subQ2=sQuery(id+"F6.wireOp",EDGE,"E56");Q49=makeQuery(id+"F7.boolean.opBoolean","COPY",EDGE,{"disambiguationData":[TD([makeQuery(id+"F1.opExtrude","SWEPT_FACE",FACE,{"disambiguationData":[OSD([subQ0])]})])],"derivedFrom":makeQuery(id+"F7.opExtrude","SWEPT_EDGE",EDGE,{"disambiguationData":[OSD([subQ1,subQ2])]})});}
            var Q50;
            {var subQ0=sQuery(id+"F0.wireOp",EDGE,"E5");var subQ1=sQuery(id+"F6.wireOp",EDGE,"E34");var subQ2=sQuery(id+"F6.wireOp",EDGE,"E56");Q50=makeQuery(id+"F7.boolean.opBoolean","COPY",EDGE,{"disambiguationData":[TD([makeQuery(id+"F1.opExtrude","SWEPT_FACE",FACE,{"disambiguationData":[OSD([subQ0])]})])],"derivedFrom":makeQuery(id+"F7.opExtrude","SWEPT_EDGE",EDGE,{"disambiguationData":[OSD([subQ1,subQ2])]})});}
            var Q51;
            {var subQ0=sQuery(id+"F0.wireOp",EDGE,"E5");var subQ1=sQuery(id+"F6.wireOp",EDGE,"E55");var subQ2=sQuery(id+"F6.wireOp",EDGE,"E36");Q51=makeQuery(id+"F7.boolean.opBoolean","COPY",EDGE,{"disambiguationData":[TD([makeQuery(id+"F1.opExtrude","SWEPT_FACE",FACE,{"disambiguationData":[OSD([subQ0])]})])],"derivedFrom":makeQuery(id+"F7.opExtrude","SWEPT_EDGE",EDGE,{"disambiguationData":[OSD([subQ2,subQ1])]})});}
            var Q52;
            {var subQ0=sQuery(id+"F0.wireOp",EDGE,"E5");var subQ1=sQuery(id+"F6.wireOp",EDGE,"E55");var subQ2=sQuery(id+"F6.wireOp",EDGE,"E37");Q52=makeQuery(id+"F7.boolean.opBoolean","COPY",EDGE,{"disambiguationData":[TD([makeQuery(id+"F1.opExtrude","SWEPT_FACE",FACE,{"disambiguationData":[OSD([subQ0])]})])],"derivedFrom":makeQuery(id+"F7.opExtrude","SWEPT_EDGE",EDGE,{"disambiguationData":[OSD([subQ2,subQ1])]})});}
            var Q53;
            {var subQ0=sQuery(id+"F0.wireOp",EDGE,"E5");var subQ1=sQuery(id+"F6.wireOp",EDGE,"E39");var subQ2=sQuery(id+"F6.wireOp",EDGE,"E54");Q53=makeQuery(id+"F7.boolean.opBoolean","COPY",EDGE,{"disambiguationData":[TD([makeQuery(id+"F1.opExtrude","SWEPT_FACE",FACE,{"disambiguationData":[OSD([subQ0])]})])],"derivedFrom":makeQuery(id+"F7.opExtrude","SWEPT_EDGE",EDGE,{"disambiguationData":[OSD([subQ1,subQ2])]})});}
            var Q54;
            {var subQ0=sQuery(id+"F0.wireOp",EDGE,"E5");var subQ1=sQuery(id+"F6.wireOp",EDGE,"E54");var subQ2=sQuery(id+"F6.wireOp",EDGE,"E58");Q54=makeQuery(id+"F7.boolean.opBoolean","COPY",EDGE,{"disambiguationData":[TD([makeQuery(id+"F1.opExtrude","SWEPT_FACE",FACE,{"disambiguationData":[OSD([subQ0])]})])],"derivedFrom":makeQuery(id+"F7.opExtrude","SWEPT_EDGE",EDGE,{"disambiguationData":[OSD([subQ1,subQ2])]})});}
            var Q55;
            {var subQ0=sQuery(id+"F0.wireOp",EDGE,"E5");var subQ1=sQuery(id+"F6.wireOp",EDGE,"E41");var subQ2=sQuery(id+"F6.wireOp",EDGE,"E53");Q55=makeQuery(id+"F7.boolean.opBoolean","COPY",EDGE,{"disambiguationData":[TD([makeQuery(id+"F1.opExtrude","SWEPT_FACE",FACE,{"disambiguationData":[OSD([subQ0])]})])],"derivedFrom":makeQuery(id+"F7.opExtrude","SWEPT_EDGE",EDGE,{"disambiguationData":[OSD([subQ1,subQ2])]})});}
            var Q56;
            {var subQ0=sQuery(id+"F0.wireOp",EDGE,"E5");var subQ1=sQuery(id+"F6.wireOp",EDGE,"E42");var subQ2=sQuery(id+"F6.wireOp",EDGE,"E53");Q56=makeQuery(id+"F7.boolean.opBoolean","COPY",EDGE,{"disambiguationData":[TD([makeQuery(id+"F1.opExtrude","SWEPT_FACE",FACE,{"disambiguationData":[OSD([subQ0])]})])],"derivedFrom":makeQuery(id+"F7.opExtrude","SWEPT_EDGE",EDGE,{"disambiguationData":[OSD([subQ1,subQ2])]})});}
            var Q57;
            {var subQ0=sQuery(id+"F0.wireOp",EDGE,"E5");var subQ1=sQuery(id+"F6.wireOp",EDGE,"E45");var subQ2=sQuery(id+"F6.wireOp",EDGE,"E52");Q57=makeQuery(id+"F7.boolean.opBoolean","COPY",EDGE,{"disambiguationData":[TD([makeQuery(id+"F1.opExtrude","SWEPT_FACE",FACE,{"disambiguationData":[OSD([subQ0])]})])],"derivedFrom":makeQuery(id+"F7.opExtrude","SWEPT_EDGE",EDGE,{"disambiguationData":[OSD([subQ1,subQ2])]})});}
            var Q58;
            {var subQ0=sQuery(id+"F0.wireOp",EDGE,"E5");var subQ1=sQuery(id+"F6.wireOp",EDGE,"E44");var subQ2=sQuery(id+"F6.wireOp",EDGE,"E52");Q58=makeQuery(id+"F7.boolean.opBoolean","COPY",EDGE,{"disambiguationData":[TD([makeQuery(id+"F1.opExtrude","SWEPT_FACE",FACE,{"disambiguationData":[OSD([subQ0])]})])],"derivedFrom":makeQuery(id+"F7.opExtrude","SWEPT_EDGE",EDGE,{"disambiguationData":[OSD([subQ1,subQ2])]})});}
            var Q59;
            {var subQ0=sQuery(id+"F0.wireOp",EDGE,"E5");var subQ1=sQuery(id+"F6.wireOp",EDGE,"E48");var subQ2=sQuery(id+"F6.wireOp",EDGE,"E51");Q59=makeQuery(id+"F7.boolean.opBoolean","COPY",EDGE,{"disambiguationData":[TD([makeQuery(id+"F1.opExtrude","SWEPT_FACE",FACE,{"disambiguationData":[OSD([subQ0])]})])],"derivedFrom":makeQuery(id+"F7.opExtrude","SWEPT_EDGE",EDGE,{"disambiguationData":[OSD([subQ1,subQ2])]})});}
            var Q60;
            {var subQ0=sQuery(id+"F0.wireOp",EDGE,"E5");var subQ1=sQuery(id+"F6.wireOp",EDGE,"E47");var subQ2=sQuery(id+"F6.wireOp",EDGE,"E51");Q60=makeQuery(id+"F7.boolean.opBoolean","COPY",EDGE,{"disambiguationData":[TD([makeQuery(id+"F1.opExtrude","SWEPT_FACE",FACE,{"disambiguationData":[OSD([subQ0])]})])],"derivedFrom":makeQuery(id+"F7.opExtrude","SWEPT_EDGE",EDGE,{"disambiguationData":[OSD([subQ1,subQ2])]})});}
            var Q61;
            {var subQ0=sQuery(id+"F0.wireOp",EDGE,"E5");var subQ1=sQuery(id+"F6.wireOp",EDGE,"E50");var subQ2=sQuery(id+"F6.wireOp",EDGE,"E27");Q61=makeQuery(id+"F7.boolean.opBoolean","COPY",EDGE,{"disambiguationData":[TD([makeQuery(id+"F1.opExtrude","SWEPT_FACE",FACE,{"disambiguationData":[OSD([subQ0])]})])],"derivedFrom":makeQuery(id+"F7.opExtrude","SWEPT_EDGE",EDGE,{"disambiguationData":[OSD([subQ2,subQ1])]})});}
            fillet(context, id + "F11", {"entities" : qUnion([Q0, Q1, Q2, Q3, Q4, Q5, Q6, Q7, Q8, Q9, Q10, Q11, Q12, Q13, Q14, Q15, Q16, Q17, Q18, Q19, Q20, Q21, Q22, Q23, Q24, Q25, Q26, Q27, Q28, Q29, Q30, Q31, Q32, Q33, Q34, Q35, Q36, Q37, Q38, Q39, Q40, Q41, Q42, Q43, Q44, Q45, Q46, Q47, Q48, Q49, Q50, Q51, Q52, Q53, Q54, Q55, Q56, Q57, Q58, Q59, Q60, Q61]), "radius" : 1.52 * mm, "tangentPropagation" : true, "allowEdgeOverflow" : false});
        }
        {
            var Q0;
            Q0=makeQuery(id+"F1.opExtrude","CAP_FACE",FACE,{"disambiguationData":[OSD([sQuery(id+"F0.wireOp",EDGE,"E2"),sQuery(id+"F0.wireOp",EDGE,"E3"),sQuery(id+"F0.wireOp",EDGE,"E4"),sQuery(id+"F0.wireOp",EDGE,"E5")])],"isStart":true});
            var Q1;
            Q1=makeQuery(id+"F3.opShell","OFFSET_FACE",FACE,{"disambiguationData":[OSD([sQuery(id+"F0.wireOp",EDGE,"E2"),sQuery(id+"F0.wireOp",EDGE,"E3"),sQuery(id+"F0.wireOp",EDGE,"E4"),sQuery(id+"F0.wireOp",EDGE,"E5")])]});
            chamfer(context, id + "F12", {"entities" : qUnion([Q0, Q1]), "width" : 1.27 * mm, "tangentPropagation" : true});
        }
        {
            var Q0;
            Q0=makeQuery(id+"F7.boolean.opBoolean","INTERSECT",EDGE,{"derivedFrom":[makeQuery(id+"F1.opExtrude","SWEPT_FACE",FACE,{"disambiguationData":[OSD([sQuery(id+"F0.wireOp",EDGE,"E3")])]}),makeQuery(id+"F7.opExtrude","SWEPT_FACE",FACE,{"disambiguationData":[OSD([sQuery(id+"F6.wireOp",EDGE,"E27")])]})]});
            var Q1;
            Q1=makeQuery(id+"F7.boolean.opBoolean","COPY",FACE,{"derivedFrom":makeQuery(id+"F7.opExtrude","SWEPT_FACE",FACE,{"disambiguationData":[OSD([sQuery(id+"F6.wireOp",EDGE,"E23")])]})});
            var Q2;
            Q2=makeQuery(id+"F7.boolean.opBoolean","INTERSECT",EDGE,{"derivedFrom":[makeQuery(id+"F3.opShell","OFFSET_FACE",FACE,{"disambiguationData":[OSD([sQuery(id+"F0.wireOp",EDGE,"E2")])]}),makeQuery(id+"F7.opExtrude","SWEPT_FACE",FACE,{"disambiguationData":[OSD([sQuery(id+"F6.wireOp",EDGE,"E28")])]})]});
            chamfer(context, id + "F13", {"entities" : qUnion([Q0, Q1, Q2]), "width" : 0.64 * mm, "tangentPropagation" : true});
        }
    });
